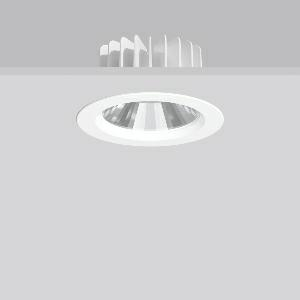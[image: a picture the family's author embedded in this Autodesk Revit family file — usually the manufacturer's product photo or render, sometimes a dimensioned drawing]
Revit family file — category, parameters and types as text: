
# Revit family: ledona_round_ip65_901524_002_2_76_d099
name_source: partatom
category: Lighting Fixtures
units: mm (PartAtom-declared; Revit-internal decimal feet)

## family parameters
Cut with Voids When Loaded = No
Host = Face
Light Source = No
Part Type = Normal
Room Calculation Point = No
Round Connector Dimension = Use Diameter
Shared = No

## types (1)
- TuneableWhite 846 (1 x LED Modul 846, 1350 lm, 4600)
    Apparent Load = 16 VA
    CIE Flux Codes = 92 99 100 100 100
    Color Rendering = 80
    Color Temperature = 4600
    Default Elevation = 1800 mm
    Height = 0 mm  [stored 0 ft]
    Lamp = 1 x LED Modul 846
    Lamp Light Flux = 1350 lm
    Lamp count = 1
    Length = 140 mm  [stored 0.459318 ft]
    Lifetime = 50000 h
    Luminous efficacy = 84 lm/W
    Manufacturer = RZB
    ModVariant = No
    Model = 901524.002.2.76
    Mounting Place = Ceiling
    Mounting Type = Recessed
    Number of Poles = 1
    OnlyDefault = Yes
    Power Factor = 1
    Product Name = LEDONA round IP65
    Product group = Recessed downlights
    ProductGroupID = 402
    Protection Class = Protection class II
    Protection Degree = IP 65
    RLX_Detail_Level = 1
    RLX_Emergency_Light_Flux = 0 lm
    RLX_Emergency_Type = 0
    RLX_Emergency_Type_DB = No
    RlxData = <blob elided: 39249 chars, md5=15706fea>
    Socket = socket
    Standby Power = 0 W
    System Light Flux = 1350 lm
    System Power = 16 W
    Type Comments = TuneableWhite 846
    Type Image = 901346.002.jpg
    URL = http://relux.com
    VarID = tuneablewhite_846
    Voltage = 230 V
    Voltage Range = 220-240 V
    Weight = 0.00 kg
    Width = 0 mm  [stored 0 ft]

note: [stored X ft] marks values corroborated as IEEE doubles in the binary element streams (Revit-internal decimal feet)

## geometry (parser evidence)
native form markers: Blend x4, Sweep x10
no freeform markers — native parametric forms only
